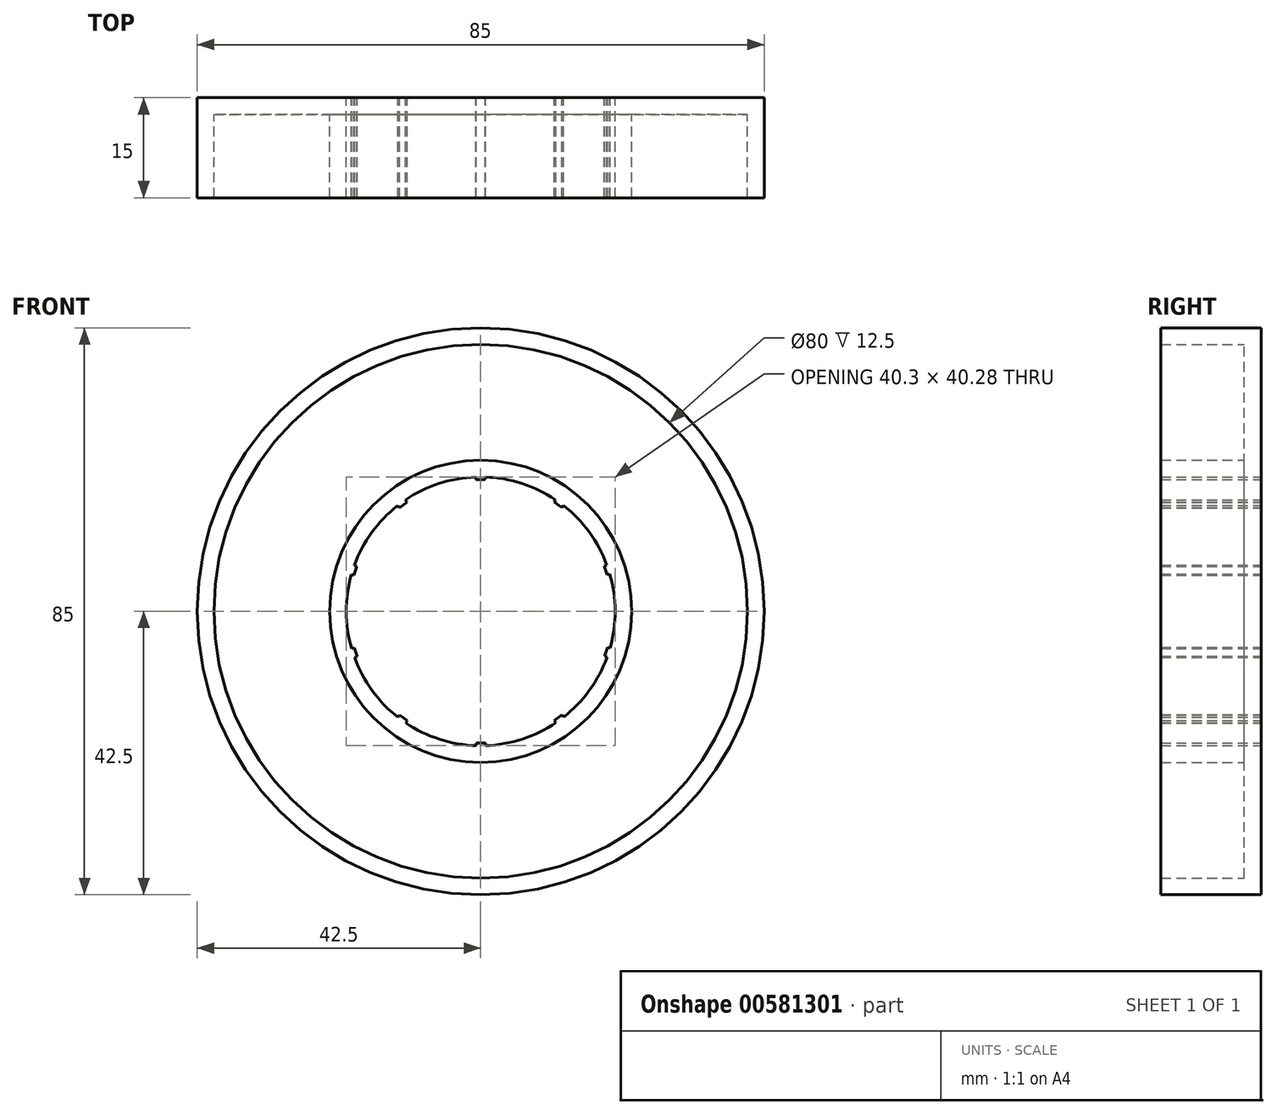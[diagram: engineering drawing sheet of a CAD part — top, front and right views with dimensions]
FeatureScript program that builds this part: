
annotation { "Feature Type Name" : "Feature", "Feature Type Description" : "" }
export const myFeature = defineFeature(function(context is Context, id is Id, definition is map)
    precondition{}
    {
        {
            var Q0;
            Q0=qCreatedBy(makeId("Front.planeOp"),FACE);
            var sketch = newSketch(context, id + "F0", { "sketchPlane" : qUnion([Q0])});
            skCircle(sketch, "E0", {"center": v(0, 0) * mm, "radius": 42.5 * mm});
            skCircle(sketch, "E1", {"center": v(0, 0) * mm, "radius": 20.15 * mm});
            skSolve(sketch);
        }
        {
            var Q0;
            Q0=makeQuery(id+"F0.imprint","IMPRINT",FACE,{"disambiguationData":[TD([[makeQuery(id+"F0.imprint","IMPRINT",EDGE,{"derivedFrom":sQuery(id+"F0.wireOp",EDGE,"E0")}),1.0]])]});
            extrude(context, id + "F1", {"entities" : qUnion([Q0]), "depth" : 15 * mm, "offsetDistance" : 25 * mm});
        }
        {
            var Q0;
            Q0=qCreatedBy(makeId("Front.planeOp"),FACE);
            var sketch = newSketch(context, id + "F2", { "sketchPlane" : qUnion([Q0])});
            skLineSegment(sketch, "E2.bottom", {"start": v(-0.74, 19.72) * mm, "end": v(0.68, 19.72) * mm});
            skLineSegment(sketch, "E2.top", {"start": v(-0.74, 21.72) * mm, "end": v(0.67, 21.72) * mm});
            skLineSegment(sketch, "E2.left", {"start": v(-0.74, 19.72) * mm, "end": v(-0.74, 21.72) * mm});
            skLineSegment(sketch, "E2.right", {"start": v(0.68, 19.72) * mm, "end": v(0.67, 21.72) * mm});
            skSolve(sketch);
        }
        {
            var Q0;
            Q0 = qSketchRegion(id + "F2", true);
            extrude(context, id + "F3", {"entities" : qUnion([Q0]), "depth" : 15 * mm, "offsetDistance" : 25 * mm});
        }
        {
            var Q0;
            Q0=makeQuery(id+"F3.opExtrude","SWEPT_BODY",BODY,{"disambiguationData":[OSD([sQuery(id+"F2.wireOp",EDGE,"E2.bottom"),sQuery(id+"F2.wireOp",EDGE,"E2.top"),sQuery(id+"F2.wireOp",EDGE,"E2.left"),sQuery(id+"F2.wireOp",EDGE,"E2.right")])]});
            var Q1;
            Q1=makeQuery(id+"F1.opExtrude","CAP_EDGE",EDGE,{"disambiguationData":[OSD([sQuery(id+"F0.wireOp",EDGE,"E1")])],"isStart":false});
            circularPattern(context, id + "F4", {"entities" : qUnion([Q0]), "axis" : qUnion([Q1]), "angle" : 360 * degree, "instanceCount" : 10, "equalSpace" : true});
        }
        {
            var Q0;
            Q0=makeQuery(id+"F1.opExtrude","SWEPT_BODY",BODY,{"disambiguationData":[OSD([sQuery(id+"F0.wireOp",EDGE,"E0"),sQuery(id+"F0.wireOp",EDGE,"E1")])]});
            var Q1;
            Q1=makeQuery(id+"F3.opExtrude","SWEPT_BODY",BODY,{"disambiguationData":[OSD([sQuery(id+"F2.wireOp",EDGE,"E2.bottom"),sQuery(id+"F2.wireOp",EDGE,"E2.top"),sQuery(id+"F2.wireOp",EDGE,"E2.left"),sQuery(id+"F2.wireOp",EDGE,"E2.right")])]});
            var Q2;
            Q2=makeQuery(id+"F4.opPattern","COPY",BODY,{"derivedFrom":makeQuery(id+"F3.opExtrude","SWEPT_BODY",BODY,{"disambiguationData":[OSD([sQuery(id+"F2.wireOp",EDGE,"E2.bottom"),sQuery(id+"F2.wireOp",EDGE,"E2.top"),sQuery(id+"F2.wireOp",EDGE,"E2.left"),sQuery(id+"F2.wireOp",EDGE,"E2.right")])]}),"instanceName":"1"});
            var Q3;
            Q3=makeQuery(id+"F4.opPattern","COPY",BODY,{"derivedFrom":makeQuery(id+"F3.opExtrude","SWEPT_BODY",BODY,{"disambiguationData":[OSD([sQuery(id+"F2.wireOp",EDGE,"E2.bottom"),sQuery(id+"F2.wireOp",EDGE,"E2.top"),sQuery(id+"F2.wireOp",EDGE,"E2.left"),sQuery(id+"F2.wireOp",EDGE,"E2.right")])]}),"instanceName":"2"});
            var Q4;
            Q4=makeQuery(id+"F4.opPattern","COPY",BODY,{"derivedFrom":makeQuery(id+"F3.opExtrude","SWEPT_BODY",BODY,{"disambiguationData":[OSD([sQuery(id+"F2.wireOp",EDGE,"E2.bottom"),sQuery(id+"F2.wireOp",EDGE,"E2.top"),sQuery(id+"F2.wireOp",EDGE,"E2.left"),sQuery(id+"F2.wireOp",EDGE,"E2.right")])]}),"instanceName":"9"});
            var Q5;
            Q5=makeQuery(id+"F4.opPattern","COPY",BODY,{"derivedFrom":makeQuery(id+"F3.opExtrude","SWEPT_BODY",BODY,{"disambiguationData":[OSD([sQuery(id+"F2.wireOp",EDGE,"E2.bottom"),sQuery(id+"F2.wireOp",EDGE,"E2.top"),sQuery(id+"F2.wireOp",EDGE,"E2.left"),sQuery(id+"F2.wireOp",EDGE,"E2.right")])]}),"instanceName":"7"});
            var Q6;
            Q6=makeQuery(id+"F4.opPattern","COPY",BODY,{"derivedFrom":makeQuery(id+"F3.opExtrude","SWEPT_BODY",BODY,{"disambiguationData":[OSD([sQuery(id+"F2.wireOp",EDGE,"E2.bottom"),sQuery(id+"F2.wireOp",EDGE,"E2.top"),sQuery(id+"F2.wireOp",EDGE,"E2.left"),sQuery(id+"F2.wireOp",EDGE,"E2.right")])]}),"instanceName":"5"});
            var Q7;
            Q7=makeQuery(id+"F4.opPattern","COPY",BODY,{"derivedFrom":makeQuery(id+"F3.opExtrude","SWEPT_BODY",BODY,{"disambiguationData":[OSD([sQuery(id+"F2.wireOp",EDGE,"E2.bottom"),sQuery(id+"F2.wireOp",EDGE,"E2.top"),sQuery(id+"F2.wireOp",EDGE,"E2.left"),sQuery(id+"F2.wireOp",EDGE,"E2.right")])]}),"instanceName":"3"});
            var Q8;
            Q8=makeQuery(id+"F4.opPattern","COPY",BODY,{"derivedFrom":makeQuery(id+"F3.opExtrude","SWEPT_BODY",BODY,{"disambiguationData":[OSD([sQuery(id+"F2.wireOp",EDGE,"E2.bottom"),sQuery(id+"F2.wireOp",EDGE,"E2.top"),sQuery(id+"F2.wireOp",EDGE,"E2.left"),sQuery(id+"F2.wireOp",EDGE,"E2.right")])]}),"instanceName":"4"});
            var Q9;
            Q9=makeQuery(id+"F4.opPattern","COPY",BODY,{"derivedFrom":makeQuery(id+"F3.opExtrude","SWEPT_BODY",BODY,{"disambiguationData":[OSD([sQuery(id+"F2.wireOp",EDGE,"E2.bottom"),sQuery(id+"F2.wireOp",EDGE,"E2.top"),sQuery(id+"F2.wireOp",EDGE,"E2.left"),sQuery(id+"F2.wireOp",EDGE,"E2.right")])]}),"instanceName":"6"});
            var Q10;
            Q10=makeQuery(id+"F4.opPattern","COPY",BODY,{"derivedFrom":makeQuery(id+"F3.opExtrude","SWEPT_BODY",BODY,{"disambiguationData":[OSD([sQuery(id+"F2.wireOp",EDGE,"E2.bottom"),sQuery(id+"F2.wireOp",EDGE,"E2.top"),sQuery(id+"F2.wireOp",EDGE,"E2.left"),sQuery(id+"F2.wireOp",EDGE,"E2.right")])]}),"instanceName":"8"});
            booleanBodies(context, id + "F5", {"operationType" : BooleanOperationType.UNION, "tools" : qUnion([Q0, Q1, Q2, Q3, Q4, Q5, Q6, Q7, Q8, Q9, Q10])});
        }
        {
            var Q0;
            {var subQ0=makeQuery(id+"F3.opExtrude","CAP_FACE",FACE,{"disambiguationData":[OSD([sQuery(id+"F2.wireOp",EDGE,"E2.bottom"),sQuery(id+"F2.wireOp",EDGE,"E2.top"),sQuery(id+"F2.wireOp",EDGE,"E2.left"),sQuery(id+"F2.wireOp",EDGE,"E2.right")])],"isStart":false});Q0=makeQuery(id+"F5.opBoolean","MERGE",FACE,{"derivedFrom":[makeQuery(id+"F1.opExtrude","CAP_FACE",FACE,{"disambiguationData":[OSD([sQuery(id+"F0.wireOp",EDGE,"E0"),sQuery(id+"F0.wireOp",EDGE,"E1")])],"isStart":false}),subQ0,makeQuery(id+"F4.opPattern","COPY",FACE,{"derivedFrom":subQ0,"instanceName":"1"}),makeQuery(id+"F4.opPattern","COPY",FACE,{"derivedFrom":subQ0,"instanceName":"2"}),makeQuery(id+"F4.opPattern","COPY",FACE,{"derivedFrom":subQ0,"instanceName":"3"}),makeQuery(id+"F4.opPattern","COPY",FACE,{"derivedFrom":subQ0,"instanceName":"4"}),makeQuery(id+"F4.opPattern","COPY",FACE,{"derivedFrom":subQ0,"instanceName":"5"}),makeQuery(id+"F4.opPattern","COPY",FACE,{"derivedFrom":subQ0,"instanceName":"6"}),makeQuery(id+"F4.opPattern","COPY",FACE,{"derivedFrom":subQ0,"instanceName":"7"}),makeQuery(id+"F4.opPattern","COPY",FACE,{"derivedFrom":subQ0,"instanceName":"8"}),makeQuery(id+"F4.opPattern","COPY",FACE,{"derivedFrom":subQ0,"instanceName":"9"})]});}
            shell(context, id + "F6", {"entities" : qUnion([Q0]), "thickness" : 2.5 * mm});
        }
    });
